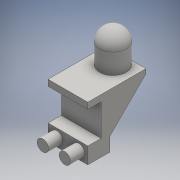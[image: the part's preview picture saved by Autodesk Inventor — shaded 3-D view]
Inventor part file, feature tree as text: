
AUTODESK INVENTOR PART (.ipt)
format: ipt  version: 2016 (Build 200138000, 138)  size: 143,872 bytes
history: native  units: mm
features: extrude x3, sketch x3, fillet x1
ambient origin geometry x8: Origin, YZ Plane, XZ Plane, XY Plane, X Axis, Y Axis, Z Axis, Center Point
bodies: Solid1 (feature_tree)
feature tree (7):
  extrude  "Extrusion1"  Depth=1.5mm
  extrude  "Extrusion2"  TaperAngle=45.0deg  [1 undecoded]
  fillet  "Fillet1"  Radius=5.2mm
  extrude  "Extrusion3"  TaperAngle=0.0deg  [1 undecoded]
  sketch  "Sketch1"  dims[d0=3.6mm d1=1.5mm]
  sketch  "Sketch2"  dims[d2=6.6mm d3=45.0deg d4=5.2mm]
  sketch  "Sketch3"  dims[d6=2.7mm d7=0.0mm d8=1.0mm d9=0.5mm d10=4.5mm d11=0.0mm d12=3.0mm d13=3.8mm d14=0.0mm d15=1.5mm d16=1.3mm d17=1.3mm d18=5.2mm d19=1.25mm d20=1.25mm d21=5.2mm d22=1.6mm d23=0.0mm]
note: 2 required parameter values undecoded (feature->parameter linkage not recoverable at this tier; creation-order binding heuristic only, values carry confidence <= 0.55)
